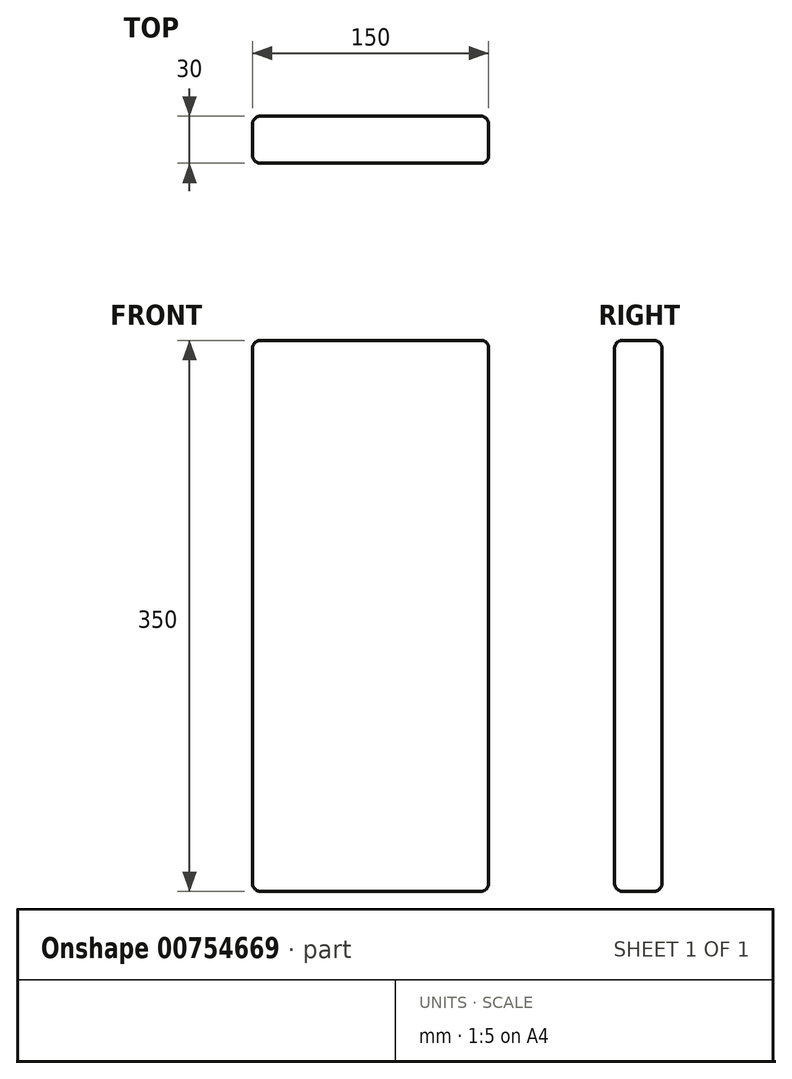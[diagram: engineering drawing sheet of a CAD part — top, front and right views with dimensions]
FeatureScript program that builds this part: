
annotation { "Feature Type Name" : "Feature", "Feature Type Description" : "" }
export const myFeature = defineFeature(function(context is Context, id is Id, definition is map)
    precondition{}
    {
        {
            var Q0;
            Q0=qCreatedBy(makeId("Front.planeOp"),FACE);
            var sketch = newSketch(context, id + "F0", { "sketchPlane" : qUnion([Q0])});
            skLineSegment(sketch, "E0.bottom", {"start": v(75, -175) * mm, "end": v(-75, -175) * mm});
            skLineSegment(sketch, "E0.top", {"start": v(75, 175) * mm, "end": v(-75, 175) * mm});
            skLineSegment(sketch, "E0.left", {"start": v(75, -175) * mm, "end": v(75, 175) * mm});
            skLineSegment(sketch, "E0.right", {"start": v(-75, -175) * mm, "end": v(-75, 175) * mm});
            skPoint(sketch, "E0.middle", {"position": v(0, 0) * mm});
            skSolve(sketch);
        }
        {
            var Q0;
            Q0=makeQuery(id+"F0.imprint","IMPRINT",FACE,{"disambiguationData":[TD([[makeQuery(id+"F0.imprint","IMPRINT",EDGE,{"derivedFrom":sQuery(id+"F0.wireOp",EDGE,"E0.bottom")}),-1.0]])]});
            extrude(context, id + "F1", {"entities" : qUnion([Q0]), "depth" : 30 * mm, "offsetDistance" : 25 * mm});
        }
        {
            var Q0;
            Q0=makeQuery(id+"F1.opExtrude","CAP_FACE",FACE,{"disambiguationData":[OSD([sQuery(id+"F0.wireOp",EDGE,"E0.bottom"),sQuery(id+"F0.wireOp",EDGE,"E0.top"),sQuery(id+"F0.wireOp",EDGE,"E0.left"),sQuery(id+"F0.wireOp",EDGE,"E0.right")])],"isStart":false});
            var Q1;
            Q1=makeQuery(id+"F1.opExtrude","CAP_FACE",FACE,{"disambiguationData":[OSD([sQuery(id+"F0.wireOp",EDGE,"E0.bottom"),sQuery(id+"F0.wireOp",EDGE,"E0.top"),sQuery(id+"F0.wireOp",EDGE,"E0.left"),sQuery(id+"F0.wireOp",EDGE,"E0.right")])],"isStart":true});
            var Q2;
            Q2=makeQuery(id+"F1.opExtrude","SWEPT_FACE",FACE,{"disambiguationData":[OSD([sQuery(id+"F0.wireOp",EDGE,"E0.left")])]});
            var Q3;
            Q3=makeQuery(id+"F1.opExtrude","SWEPT_FACE",FACE,{"disambiguationData":[OSD([sQuery(id+"F0.wireOp",EDGE,"E0.top")])]});
            var Q4;
            Q4=makeQuery(id+"F1.opExtrude","SWEPT_FACE",FACE,{"disambiguationData":[OSD([sQuery(id+"F0.wireOp",EDGE,"E0.bottom")])]});
            fillet(context, id + "F2", {"entities" : qUnion([Q0, Q1, Q2, Q3, Q4]), "radius" : 5 * mm, "tangentPropagation" : true, "allowEdgeOverflow" : false});
        }
    });
